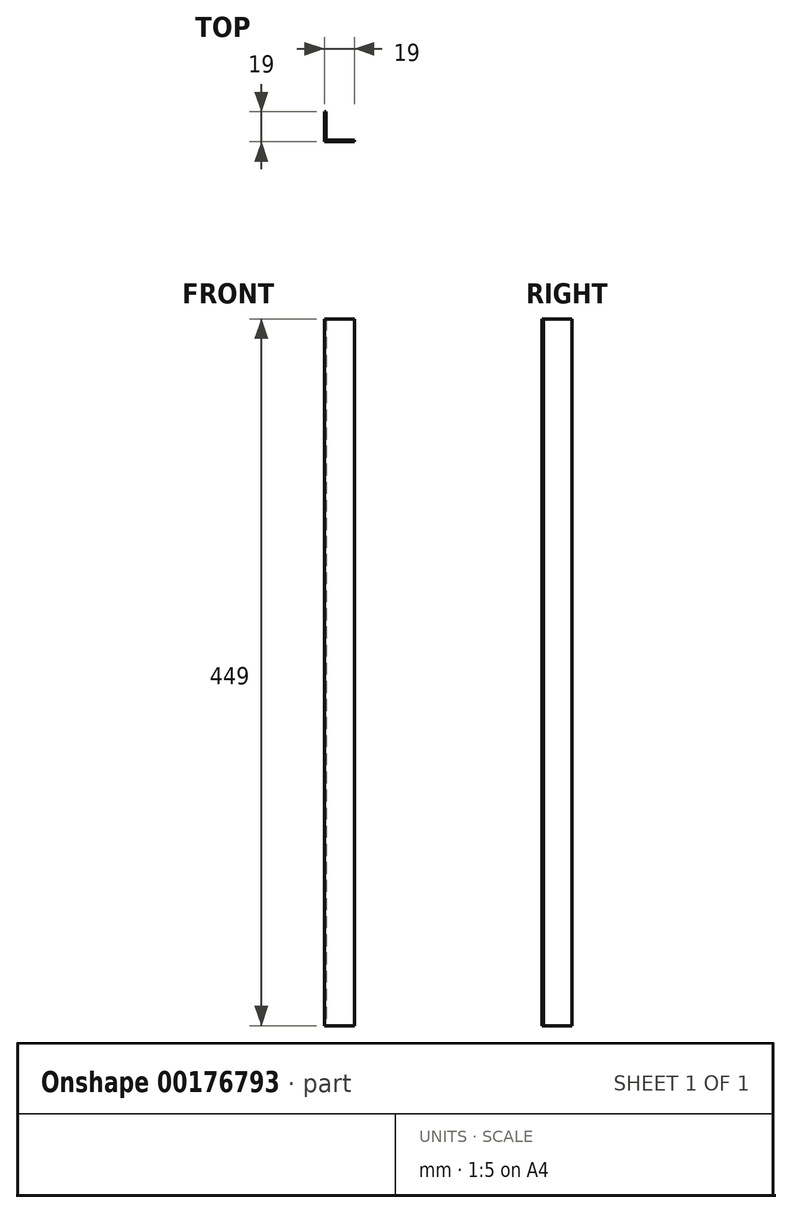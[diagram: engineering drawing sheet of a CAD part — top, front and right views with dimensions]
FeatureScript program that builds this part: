
annotation { "Feature Type Name" : "Feature", "Feature Type Description" : "" }
export const myFeature = defineFeature(function(context is Context, id is Id, definition is map)
    precondition{}
    {
        {
            var Q0;
            Q0=qCreatedBy(makeId("Top.planeOp"),FACE);
            var sketch = newSketch(context, id + "F0", { "sketchPlane" : qUnion([Q0])});
            skLineSegment(sketch, "E0", {"start": v(-4.62, -4.99) * mm, "end": v(14.38, -4.99) * mm});
            skLineSegment(sketch, "E1", {"start": v(-4.62, -4.99) * mm, "end": v(-4.62, 14.01) * mm});
            skLineSegment(sketch, "E2", {"start": v(-4.62, 14.01) * mm, "end": v(-3.62, 14.01) * mm});
            skLineSegment(sketch, "E3", {"start": v(-3.62, 14.01) * mm, "end": v(-3.62, -3.99) * mm});
            skLineSegment(sketch, "E4", {"start": v(-3.62, -3.99) * mm, "end": v(14.38, -3.99) * mm});
            skLineSegment(sketch, "E5", {"start": v(14.38, -3.99) * mm, "end": v(14.38, -4.99) * mm});
            skSolve(sketch);
        }
        {
            var Q0;
            Q0=makeQuery(id+"F0.imprint","IMPRINT",FACE,{"disambiguationData":[TD([[makeQuery(id+"F0.imprint","IMPRINT",EDGE,{"derivedFrom":sQuery(id+"F0.wireOp",EDGE,"E0")}),1.0]])]});
            var Q1;
            Q1=sQuery(id+"F0.wireOp",EDGE,"E0");
            var Q2;
            Q2=sQuery(id+"F0.wireOp",EDGE,"E1");
            var Q3;
            Q3=sQuery(id+"F0.wireOp",EDGE,"E2");
            var Q4;
            Q4=sQuery(id+"F0.wireOp",EDGE,"E3");
            var Q5;
            Q5=sQuery(id+"F0.wireOp",EDGE,"E4");
            var Q6;
            Q6=sQuery(id+"F0.wireOp",EDGE,"E5");
            extrude(context, id + "F1", {"entities" : qUnion([Q0]), "surfaceEntities" : qUnion([Q1, Q2, Q3, Q4, Q5, Q6]), "depth" : 449 * mm});
        }
    });
